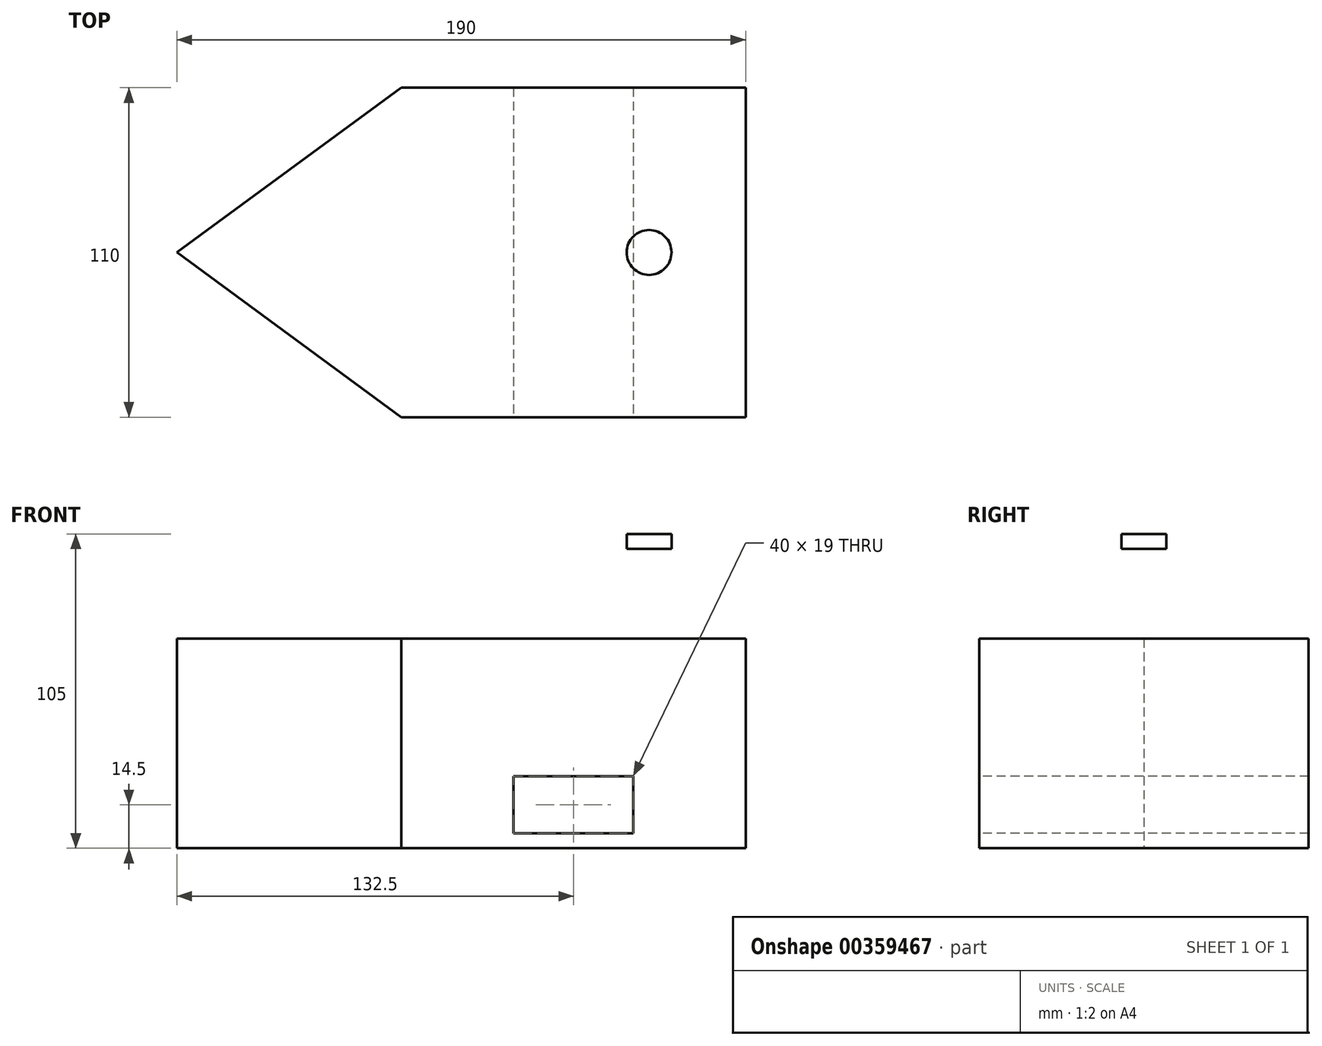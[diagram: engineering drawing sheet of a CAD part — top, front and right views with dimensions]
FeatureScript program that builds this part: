
annotation { "Feature Type Name" : "Feature", "Feature Type Description" : "" }
export const myFeature = defineFeature(function(context is Context, id is Id, definition is map)
    precondition{}
    {
        {
            var Q0;
            Q0=qCreatedBy(makeId("Top.planeOp"),FACE);
            var sketch = newSketch(context, id + "F0", { "sketchPlane" : qUnion([Q0])});
            skLineSegment(sketch, "E0", {"start": v(0, 55) * mm, "end": v(0, -55) * mm});
            skLineSegment(sketch, "E1", {"start": v(-115, 55) * mm, "end": v(0, 55) * mm});
            skLineSegment(sketch, "E2", {"start": v(-115, -55) * mm, "end": v(0, -55) * mm});
            skLineSegment(sketch, "E3", {"start": v(-115, 55) * mm, "end": v(-115, -55) * mm});
            skLineSegment(sketch, "E4", {"start": v(0, 0) * mm, "end": v(-115, 0) * mm});
            skLineSegment(sketch, "E5", {"start": v(-115, 0) * mm, "end": v(-190, 0) * mm});
            skLineSegment(sketch, "E6", {"start": v(-115, 55) * mm, "end": v(-190, 0) * mm});
            skLineSegment(sketch, "E7", {"start": v(-115, -55) * mm, "end": v(-190, 0) * mm});
            skSolve(sketch);
        }
        {
            var Q0;
            Q0 = qSketchRegion(id + "F0", true);
            extrude(context, id + "F1", {"entities" : qUnion([Q0]), "depth" : 70 * mm, "offsetDistance" : 25 * mm});
        }
        {
            var Q0;
            Q0=makeQuery(id+"F1.opExtrude","SWEPT_FACE",FACE,{"disambiguationData":[OSD([sQuery(id+"F0.wireOp",EDGE,"E2")])]});
            var sketch = newSketch(context, id + "F2", { "sketchPlane" : qUnion([Q0])});
            skLineSegment(sketch, "E8", {"start": v(-57.5, 0) * mm, "end": v(-57.5, 5) * mm});
            skLineSegment(sketch, "E9.bottom", {"start": v(-77.5, 5) * mm, "end": v(-37.5, 5) * mm});
            skLineSegment(sketch, "E9.top", {"start": v(-77.5, 24) * mm, "end": v(-37.5, 24) * mm});
            skLineSegment(sketch, "E9.left", {"start": v(-77.5, 5) * mm, "end": v(-77.5, 24) * mm});
            skLineSegment(sketch, "E9.right", {"start": v(-37.5, 5) * mm, "end": v(-37.5, 24) * mm});
            skPoint(sketch, "E9.middle", {"position": v(-57.5, 14.5) * mm});
            skSolve(sketch);
        }
        {
            var Q0;
            Q0 = qSketchRegion(id + "F2", true);
            extrude(context, id + "F3", {"entities" : qUnion([Q0]), "operationType" : NewBodyOperationType.REMOVE, "oppositeDirection" : true, "depth" : 300 * mm, "offsetDistance" : 25 * mm});
        }
        {
            var Q0;
            Q0=makeQuery(id+"F1.opExtrude","CAP_FACE",FACE,{"disambiguationData":[OSD([sQuery(id+"F0.wireOp",EDGE,"E0"),sQuery(id+"F0.wireOp",EDGE,"E1"),sQuery(id+"F0.wireOp",EDGE,"E2"),sQuery(id+"F0.wireOp",EDGE,"E6"),sQuery(id+"F0.wireOp",EDGE,"E7")])],"isStart":false});
            cPlane(context, id + "F4", {"entities" : qUnion([Q0]), "cplaneType" : CPlaneType.OFFSET, "offset" : 25 * mm, "width" : 150 * mm, "height" : 150 * mm});
        }
        {
            var Q0;
            Q0=qCreatedBy(id+"F4.planeOp",FACE);
            var sketch = newSketch(context, id + "F5", { "sketchPlane" : qUnion([Q0])});
            skLineSegment(sketch, "E10.0", {"start": v(5.5, -60.5) * mm, "end": v(5.5, 60.5) * mm});
            skLineSegment(sketch, "E10.1", {"start": v(-116.8, -60.5) * mm, "end": v(5.5, -60.5) * mm});
            skLineSegment(sketch, "E10.2", {"start": v(5.5, 60.5) * mm, "end": v(-116.8, 60.5) * mm});
            skLineSegment(sketch, "E10.3", {"start": v(-116.8, 60.5) * mm, "end": v(-199.3, 0) * mm});
            skLineSegment(sketch, "E10.4", {"start": v(-199.3, 0) * mm, "end": v(-116.8, -60.5) * mm});
            skSolve(sketch);
        }
        {
            var Q0;
            Q0 = qSketchRegion(id + "F5", true);
            extrude(context, id + "F6", {"entities" : qUnion([Q0]), "depth" : 10 * mm, "offsetDistance" : 25 * mm});
        }
        {
            var Q0;
            Q0=makeQuery(id+"F6.opExtrude","CAP_FACE",FACE,{"disambiguationData":[OSD([sQuery(id+"F5.wireOp",EDGE,"E10.0"),sQuery(id+"F5.wireOp",EDGE,"E10.1"),sQuery(id+"F5.wireOp",EDGE,"E10.2"),sQuery(id+"F5.wireOp",EDGE,"E10.3"),sQuery(id+"F5.wireOp",EDGE,"E10.4")])],"isStart":true});
            var sketch = newSketch(context, id + "F7", { "sketchPlane" : qUnion([Q0])});
            skLineSegment(sketch, "E11.0", {"start": v(-190.85, 0) * mm, "end": v(-115.16, 55.5) * mm});
            skLineSegment(sketch, "E11.1", {"start": v(-115.16, -55.5) * mm, "end": v(-190.85, 0) * mm});
            skLineSegment(sketch, "E11.2", {"start": v(-115.16, 55.5) * mm, "end": v(0.5, 55.5) * mm});
            skLineSegment(sketch, "E11.3", {"start": v(0.5, 55.5) * mm, "end": v(0.5, -55.5) * mm});
            skLineSegment(sketch, "E11.4", {"start": v(0.5, -55.5) * mm, "end": v(-115.16, -55.5) * mm});
            skSolve(sketch);
        }
        {
            var Q0;
            Q0=makeQuery(id+"F7.imprint","IMPRINT",FACE,{"disambiguationData":[TD([[makeQuery(id+"F7.imprint","IMPRINT",EDGE,{"derivedFrom":sQuery(id+"F7.wireOp",EDGE,"E11.0")}),-1.0]])]});
            extrude(context, id + "F8", {"entities" : qUnion([Q0]), "operationType" : NewBodyOperationType.REMOVE, "oppositeDirection" : true, "depth" : 5 * mm, "offsetDistance" : 25 * mm});
        }
        {
            var Q0;
            Q0=makeQuery(id+"F6.opExtrude","CAP_FACE",FACE,{"disambiguationData":[OSD([sQuery(id+"F5.wireOp",EDGE,"E10.0"),sQuery(id+"F5.wireOp",EDGE,"E10.1"),sQuery(id+"F5.wireOp",EDGE,"E10.2"),sQuery(id+"F5.wireOp",EDGE,"E10.3"),sQuery(id+"F5.wireOp",EDGE,"E10.4")])],"isStart":false});
            var sketch = newSketch(context, id + "F9", { "sketchPlane" : qUnion([Q0])});
            skCircle(sketch, "E12", {"center": v(-114.75, 0) * mm, "radius": 40 * mm});
            skLineSegment(sketch, "E13", {"start": v(-199.3, 0) * mm, "end": v(5.5, 0) * mm});
            skCircle(sketch, "E14", {"center": v(-32.26, 0) * mm, "radius": 7.5 * mm});
            skSolve(sketch);
        }
        {
            var Q0;
            {var subQ0=sQuery(id+"F9.wireOp",EDGE,"E13");var subQ1=sQuery(id+"F9.wireOp",EDGE,"E12");var subQ2=makeQuery(id+"F9.imprint","INTERSECT",VERTEX,{"disambiguationData":[OD(0.0)],"derivedFrom":[subQ1,subQ0]});Q0=makeQuery(id+"F9.imprint","IMPRINT",FACE,{"disambiguationData":[TD([[makeQuery(id+"F9.imprint","IMPRINT",EDGE,{"disambiguationData":[TD([[subQ2,1.0]])],"derivedFrom":subQ1}),1.0]])]});}
            var Q1;
            {var subQ0=sQuery(id+"F9.wireOp",EDGE,"E13");var subQ1=sQuery(id+"F9.wireOp",EDGE,"E12");var subQ2=makeQuery(id+"F9.imprint","INTERSECT",VERTEX,{"disambiguationData":[OD(0.0)],"derivedFrom":[subQ1,subQ0]});Q1=makeQuery(id+"F9.imprint","IMPRINT",FACE,{"disambiguationData":[TD([[makeQuery(id+"F9.imprint","IMPRINT",EDGE,{"disambiguationData":[TD([[subQ2,-1.0]])],"derivedFrom":subQ1}),1.0]])]});}
            var Q2;
            {var subQ0=sQuery(id+"F9.wireOp",EDGE,"E14");var subQ1=sQuery(id+"F9.wireOp",EDGE,"E13");var subQ2=makeQuery(id+"F9.imprint","INTERSECT",VERTEX,{"disambiguationData":[OD(0.0)],"derivedFrom":[subQ1,subQ0]});Q2=makeQuery(id+"F9.imprint","IMPRINT",FACE,{"disambiguationData":[TD([[makeQuery(id+"F9.imprint","IMPRINT",EDGE,{"disambiguationData":[TD([[subQ2,-1.0]])],"derivedFrom":subQ1}),-1.0]])]});}
            var Q3;
            {var subQ0=sQuery(id+"F9.wireOp",EDGE,"E14");var subQ1=sQuery(id+"F9.wireOp",EDGE,"E13");var subQ2=makeQuery(id+"F9.imprint","INTERSECT",VERTEX,{"disambiguationData":[OD(0.0)],"derivedFrom":[subQ1,subQ0]});Q3=makeQuery(id+"F9.imprint","IMPRINT",FACE,{"disambiguationData":[TD([[makeQuery(id+"F9.imprint","IMPRINT",EDGE,{"disambiguationData":[TD([[subQ2,-1.0]])],"derivedFrom":subQ1}),1.0]])]});}
            extrude(context, id + "F10", {"entities" : qUnion([Q0, Q1, Q2, Q3]), "operationType" : NewBodyOperationType.REMOVE, "oppositeDirection" : true, "depth" : 25 * mm, "offsetDistance" : 25 * mm});
        }
    });
